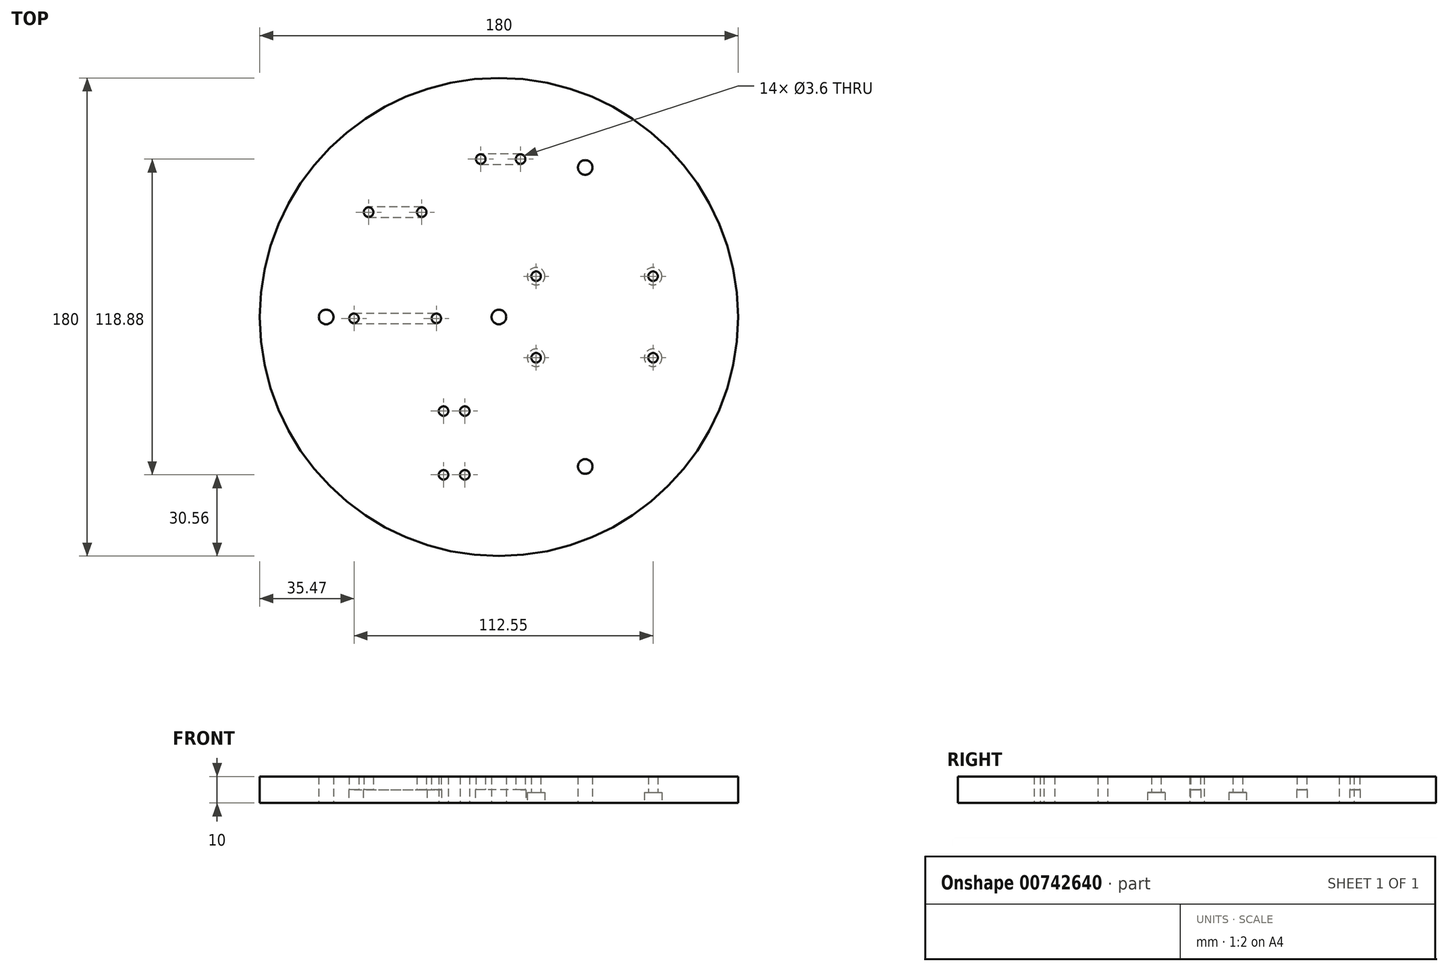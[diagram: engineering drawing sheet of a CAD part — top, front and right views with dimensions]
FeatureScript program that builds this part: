
annotation { "Feature Type Name" : "Feature", "Feature Type Description" : "" }
export const myFeature = defineFeature(function(context is Context, id is Id, definition is map)
    precondition{}
    {
        {
            var Q0;
            Q0=qCreatedBy(makeId("Top.planeOp"),FACE);
            var sketch = newSketch(context, id + "F0", { "sketchPlane" : qUnion([Q0])});
            skCircle(sketch, "E0", {"center": v(0, 0) * mm, "radius": 90 * mm});
            skLineSegment(sketch, "E1.bottom", {"start": v(22.62, 8) * mm, "end": v(49.42, 8) * mm, "construction": true});
            skLineSegment(sketch, "E1.top", {"start": v(22.62, -8) * mm, "end": v(49.42, -8) * mm, "construction": true});
            skLineSegment(sketch, "E1.left", {"start": v(22.62, 8) * mm, "end": v(22.62, -8) * mm, "construction": true});
            skLineSegment(sketch, "E1.right", {"start": v(49.42, 8) * mm, "end": v(49.42, -8) * mm, "construction": true});
            skPoint(sketch, "E1.middle", {"position": v(36.02, 0) * mm});
            skCircle(sketch, "E2", {"center": v(0, 0) * mm, "radius": 65 * mm, "construction": true});
            skPoint(sketch, "E3", {"position": v(-32.5, 56.3) * mm});
            skPoint(sketch, "E4", {"position": v(-32.5, -56.3) * mm});
            skPoint(sketch, "E5", {"position": v(65, 0) * mm});
            skPoint(sketch, "E5.positionSnap0", {"position": v(49.42, 0) * mm});
            skPoint(sketch, "E6", {"position": v(32.5, 56.3) * mm});
            skPoint(sketch, "E7", {"position": v(32.5, -56.3) * mm});
            skPoint(sketch, "E8", {"position": v(-65, 0) * mm});
            skLineSegment(sketch, "E9", {"start": v(-32.5, 56.3) * mm, "end": v(0, 0) * mm, "construction": true});
            skLineSegment(sketch, "E10", {"start": v(32.5, 56.3) * mm, "end": v(0, 0) * mm, "construction": true});
            skLineSegment(sketch, "E11", {"start": v(-65, 0) * mm, "end": v(0, 0) * mm, "construction": true});
            skLineSegment(sketch, "E12", {"start": v(-32.5, -56.3) * mm, "end": v(0, 0) * mm, "construction": true});
            skLineSegment(sketch, "E13", {"start": v(32.5, -56.3) * mm, "end": v(0, 0) * mm, "construction": true});
            skLineSegment(sketch, "E14", {"start": v(65, 0) * mm, "end": v(0, 0) * mm, "construction": true});
            skSolve(sketch);
        }
        {
            var Q0;
            Q0=qCreatedBy(makeId("Top.planeOp"),FACE);
            var sketch = newSketch(context, id + "F1", { "sketchPlane" : qUnion([Q0])});
            skLineSegment(sketch, "E15.bottom", {"start": v(-72.38, 45) * mm, "end": v(7.62, 45) * mm});
            skLineSegment(sketch, "E15.top", {"start": v(-72.38, -45) * mm, "end": v(7.62, -45) * mm});
            skLineSegment(sketch, "E15.left", {"start": v(-72.38, 45) * mm, "end": v(-72.38, -45) * mm});
            skLineSegment(sketch, "E15.right", {"start": v(7.62, 45) * mm, "end": v(7.62, -45) * mm});
            skPoint(sketch, "E16", {"position": v(-1.43, 29.7) * mm});
            skPoint(sketch, "E17", {"position": v(-1.43, -40) * mm});
            skPoint(sketch, "E18", {"position": v(-66.43, -40) * mm});
            skPoint(sketch, "E19", {"position": v(-46.03, -21.05) * mm});
            skPoint(sketch, "E20", {"position": v(-59.33, 38.95) * mm});
            skLineSegment(sketch, "E21", {"start": v(-1.43, -40) * mm, "end": v(-66.43, -40) * mm, "construction": true});
            skLineSegment(sketch, "E22", {"start": v(-66.43, -40) * mm, "end": v(-72.38, -40) * mm, "construction": true});
            skLineSegment(sketch, "E23", {"start": v(-1.43, -40) * mm, "end": v(-1.43, 29.7) * mm, "construction": true});
            skLineSegment(sketch, "E24", {"start": v(-59.33, 38.95) * mm, "end": v(-59.33, 45) * mm, "construction": true});
            skLineSegment(sketch, "E25", {"start": v(-59.33, 38.95) * mm, "end": v(-72.38, 38.95) * mm, "construction": true});
            skLineSegment(sketch, "E26", {"start": v(-46.03, -21.05) * mm, "end": v(-72.38, -21.05) * mm, "construction": true});
            skLineSegment(sketch, "E27", {"start": v(-46.03, -21.05) * mm, "end": v(-46.03, -45) * mm, "construction": true});
            skLineSegment(sketch, "E28", {"start": v(-66.43, -40) * mm, "end": v(-66.43, -45) * mm, "construction": true});
            skLineSegment(sketch, "E29", {"start": v(-1.43, 29.7) * mm, "end": v(-1.43, 45) * mm, "construction": true});
            skSolve(sketch);
        }
        {
            var Q0;
            Q0=qCreatedBy(makeId("Top.planeOp"),FACE);
            var sketch = newSketch(context, id + "F2", { "sketchPlane" : qUnion([Q0])});
            skLineSegment(sketch, "E30.bottom", {"start": v(-59.38, 49) * mm, "end": v(-6.08, 49) * mm});
            skLineSegment(sketch, "E30.top", {"start": v(-59.38, -49) * mm, "end": v(-6.08, -49) * mm});
            skLineSegment(sketch, "E30.left", {"start": v(-59.38, 49) * mm, "end": v(-59.38, -49) * mm});
            skLineSegment(sketch, "E30.right", {"start": v(-6.08, 49) * mm, "end": v(-6.08, -49) * mm});
            skPoint(sketch, "E31", {"position": v(-57, 34.97) * mm});
            skPoint(sketch, "E32", {"position": v(-8.8, 33.67) * mm});
            skPoint(sketch, "E33", {"position": v(-24, -17.13) * mm});
            skPoint(sketch, "E34", {"position": v(-51.9, -17.13) * mm});
            skPoint(sketch, "E35", {"position": v(-8.8, -41.23) * mm});
            skPoint(sketch, "E36", {"position": v(-57, -47.23) * mm});
            skSolve(sketch);
        }
        {
            var Q0;
            Q0=makeQuery(id+"F0.imprint","IMPRINT",FACE,{"disambiguationData":[TD([[makeQuery(id+"F0.imprint","IMPRINT",EDGE,{"derivedFrom":sQuery(id+"F0.wireOp",EDGE,"E0")}),1.0]])]});
            extrude(context, id + "F3", {"entities" : qUnion([Q0]), "depth" : 10 * mm, "offsetDistance" : 25 * mm});
        }
        {
            var Q0;
            Q0=sQuery(id+"F0.wireOp",VERTEX,"E6");
            var Q1;
            Q1=sQuery(id+"F0.wireOp",VERTEX,"E7");
            var Q2;
            Q2=sQuery(id+"F0.wireOp",VERTEX,"E8");
            var Q3;
            Q3=sQuery(id+"F0.wireOp",VERTEX,"E0.center");
            var Q4;
            Q4=makeQuery(id+"F3.opExtrude","SWEPT_BODY",BODY,{"disambiguationData":[OSD([sQuery(id+"F0.wireOp",EDGE,"E0")])]});
            hole(context, id + "F4", {"style" : HoleStyle.SIMPLE, "endStyle" : HoleEndStyle.BLIND, "oppositeDirection" : true, "holeDiameter" : 5.5 * mm, "majorDiameter" : 5 * mm, "holeDepth" : 30 * mm, "isTappedThrough" : true, "tappedDepth" : 10.5 * mm, "tapClearance" : 3, "locations" : qUnion([Q0, Q1, Q2, Q3]), "scope" : qUnion([Q4])});
        }
        {
            var Q0;
            Q0=makeQuery(id+"F0.imprint","IMPRINT",FACE,{"disambiguationData":[TD([[makeQuery(id+"F0.imprint","IMPRINT",EDGE,{"derivedFrom":sQuery(id+"F0.wireOp",EDGE,"E0")}),1.0]])]});
            var sketch = newSketch(context, id + "F5", { "sketchPlane" : qUnion([Q0])});
            skLineSegment(sketch, "E37.bottom", {"start": v(58.02, 15.35) * mm, "end": v(14.02, 15.35) * mm, "construction": true});
            skLineSegment(sketch, "E37.top", {"start": v(58.02, -15.35) * mm, "end": v(14.02, -15.35) * mm, "construction": true});
            skLineSegment(sketch, "E37.left", {"start": v(58.02, 15.35) * mm, "end": v(58.02, -15.35) * mm, "construction": true});
            skLineSegment(sketch, "E37.right", {"start": v(14.02, 15.35) * mm, "end": v(14.02, -15.35) * mm, "construction": true});
            skPoint(sketch, "E37.middle", {"position": v(36.02, 0) * mm});
            skSolve(sketch);
        }
        {
            var Q0;
            Q0=sQuery(id+"F5.wireOp",VERTEX,"E37.top.end");
            var Q1;
            Q1=sQuery(id+"F5.wireOp",VERTEX,"E37.top.start");
            var Q2;
            Q2=sQuery(id+"F5.wireOp",VERTEX,"E37.bottom.end");
            var Q3;
            Q3=sQuery(id+"F5.wireOp",VERTEX,"E37.bottom.start");
            var Q4;
            Q4=makeQuery(id+"F3.opExtrude","SWEPT_BODY",BODY,{"disambiguationData":[OSD([sQuery(id+"F0.wireOp",EDGE,"E0")])]});
            hole(context, id + "F6", {"style" : HoleStyle.C_BORE, "endStyle" : HoleEndStyle.THROUGH, "oppositeDirection" : true, "holeDiameter" : 3.6 * mm, "cBoreDiameter" : 6.6 * mm, "cBoreDepth" : 4 * mm, "majorDiameter" : 5 * mm, "isTappedThrough" : true, "tappedDepth" : 10.5 * mm, "tapClearance" : 3, "locations" : qUnion([Q0, Q1, Q2, Q3]), "scope" : qUnion([Q4])});
        }
        {
            var Q0;
            Q0=makeQuery(id+"F0.imprint","IMPRINT",FACE,{"disambiguationData":[TD([[makeQuery(id+"F0.imprint","IMPRINT",EDGE,{"derivedFrom":sQuery(id+"F0.wireOp",EDGE,"E0")}),1.0]])]});
            var sketch = newSketch(context, id + "F7", { "sketchPlane" : qUnion([Q0])});
            skLineSegment(sketch, "E38.bottom", {"start": v(-20.82, -35.44) * mm, "end": v(-12.82, -35.44) * mm, "construction": true});
            skLineSegment(sketch, "E38.top", {"start": v(-20.82, -59.44) * mm, "end": v(-12.82, -59.44) * mm, "construction": true});
            skLineSegment(sketch, "E38.left", {"start": v(-20.82, -35.44) * mm, "end": v(-20.82, -59.44) * mm, "construction": true});
            skLineSegment(sketch, "E38.right", {"start": v(-12.82, -35.44) * mm, "end": v(-12.82, -59.44) * mm, "construction": true});
            skPoint(sketch, "E38.middle", {"position": v(-16.82, -47.44) * mm});
            skPoint(sketch, "E39", {"position": v(-6.83, 59.44) * mm});
            skPoint(sketch, "E40", {"position": v(8.17, 59.44) * mm});
            skPoint(sketch, "E41", {"position": v(-29.03, 39.48) * mm});
            skPoint(sketch, "E42", {"position": v(-49.03, 39.48) * mm});
            skPoint(sketch, "E43", {"position": v(-54.53, -0.52) * mm});
            skPoint(sketch, "E44", {"position": v(-23.53, -0.52) * mm});
            skCircle(sketch, "E45", {"center": v(-54.53, -0.52) * mm, "radius": 2 * mm});
            skCircle(sketch, "E46", {"center": v(-23.53, -0.52) * mm, "radius": 2 * mm});
            skCircle(sketch, "E47", {"center": v(-29.03, 39.48) * mm, "radius": 2 * mm});
            skCircle(sketch, "E48", {"center": v(-49.03, 39.48) * mm, "radius": 2 * mm});
            skCircle(sketch, "E49", {"center": v(-6.83, 59.44) * mm, "radius": 2 * mm});
            skCircle(sketch, "E50", {"center": v(8.17, 59.44) * mm, "radius": 2 * mm});
            skLineSegment(sketch, "E51", {"start": v(-54.6, 1.48) * mm, "end": v(-23.53, 1.48) * mm});
            skLineSegment(sketch, "E52", {"start": v(-54.53, -2.52) * mm, "end": v(-23.53, -2.52) * mm});
            skLineSegment(sketch, "E53", {"start": v(-49.03, 37.48) * mm, "end": v(-29.03, 37.48) * mm});
            skLineSegment(sketch, "E54", {"start": v(-29.03, 41.48) * mm, "end": v(-49.03, 41.48) * mm});
            skLineSegment(sketch, "E55", {"start": v(-6.83, 57.44) * mm, "end": v(8.17, 57.44) * mm});
            skLineSegment(sketch, "E56", {"start": v(8.17, 61.44) * mm, "end": v(-6.83, 61.44) * mm});
            skSolve(sketch);
        }
        {
            var Q0;
            Q0=sQuery(id+"F7.wireOp",VERTEX,"E38.top.end");
            var Q1;
            Q1=sQuery(id+"F7.wireOp",VERTEX,"E38.top.start");
            var Q2;
            Q2=sQuery(id+"F7.wireOp",VERTEX,"E38.bottom.end");
            var Q3;
            Q3=sQuery(id+"F7.wireOp",VERTEX,"E38.bottom.start");
            var Q4;
            Q4=sQuery(id+"F7.wireOp",VERTEX,"E42");
            var Q5;
            Q5=sQuery(id+"F7.wireOp",VERTEX,"E41");
            var Q6;
            Q6=sQuery(id+"F7.wireOp",VERTEX,"E39");
            var Q7;
            Q7=sQuery(id+"F7.wireOp",VERTEX,"E40");
            var Q8;
            Q8=sQuery(id+"F7.wireOp",VERTEX,"E44");
            var Q9;
            Q9=sQuery(id+"F7.wireOp",VERTEX,"E43");
            var Q10;
            Q10=makeQuery(id+"F3.opExtrude","SWEPT_BODY",BODY,{"disambiguationData":[OSD([sQuery(id+"F0.wireOp",EDGE,"E0")])]});
            hole(context, id + "F8", {"style" : HoleStyle.SIMPLE, "endStyle" : HoleEndStyle.BLIND, "oppositeDirection" : true, "holeDiameter" : 3.6 * mm, "majorDiameter" : 5 * mm, "holeDepth" : 30 * mm, "isTappedThrough" : true, "tappedDepth" : 10.5 * mm, "tapClearance" : 3, "locations" : qUnion([Q0, Q1, Q2, Q3, Q4, Q5, Q6, Q7, Q8, Q9]), "scope" : qUnion([Q10])});
        }
        {
            var Q0;
            {var subQ0=sQuery(id+"F7.wireOp",EDGE,"E51");var subQ1=sQuery(id+"F7.wireOp",EDGE,"E45");var subQ2=makeQuery(id+"F7.imprint","INTERSECT",VERTEX,{"disambiguationData":[OD(0.0)],"derivedFrom":[subQ1,subQ0]});Q0=makeQuery(id+"F7.imprint","IMPRINT",FACE,{"disambiguationData":[TD([[makeQuery(id+"F7.imprint","IMPRINT",EDGE,{"disambiguationData":[TD([[subQ2,-1.0]])],"derivedFrom":subQ1}),1.0]])]});}
            var Q1;
            {var subQ0=sQuery(id+"F7.wireOp",EDGE,"E46");var subQ1=makeQuery(id+"F7.imprint","INTERSECT",VERTEX,{"derivedFrom":[subQ0,sQuery(id+"F7.wireOp",EDGE,"E51")]});Q1=makeQuery(id+"F7.imprint","IMPRINT",FACE,{"disambiguationData":[TD([[makeQuery(id+"F7.imprint","IMPRINT",EDGE,{"disambiguationData":[TD([[subQ1,-1.0]])],"derivedFrom":subQ0}),1.0]])]});}
            var Q2;
            {var subQ0=sQuery(id+"F7.wireOp",EDGE,"E52");Q2=makeQuery(id+"F7.imprint","IMPRINT",FACE,{"disambiguationData":[TD([[makeQuery(id+"F7.imprint","IMPRINT",EDGE,{"derivedFrom":subQ0}),1.0]])]});}
            var Q3;
            {var subQ0=sQuery(id+"F7.wireOp",EDGE,"E53");Q3=makeQuery(id+"F7.imprint","IMPRINT",FACE,{"disambiguationData":[TD([[makeQuery(id+"F7.imprint","IMPRINT",EDGE,{"derivedFrom":subQ0}),1.0]])]});}
            var Q4;
            {var subQ0=sQuery(id+"F7.wireOp",EDGE,"E48");var subQ1=makeQuery(id+"F7.imprint","INTERSECT",VERTEX,{"derivedFrom":[subQ0,sQuery(id+"F7.wireOp",EDGE,"E53")]});Q4=makeQuery(id+"F7.imprint","IMPRINT",FACE,{"disambiguationData":[TD([[makeQuery(id+"F7.imprint","IMPRINT",EDGE,{"disambiguationData":[TD([[subQ1,1.0]])],"derivedFrom":subQ0}),1.0]])]});}
            var Q5;
            {var subQ0=sQuery(id+"F7.wireOp",EDGE,"E47");var subQ1=makeQuery(id+"F7.imprint","INTERSECT",VERTEX,{"derivedFrom":[subQ0,sQuery(id+"F7.wireOp",EDGE,"E53")]});Q5=makeQuery(id+"F7.imprint","IMPRINT",FACE,{"disambiguationData":[TD([[makeQuery(id+"F7.imprint","IMPRINT",EDGE,{"disambiguationData":[TD([[subQ1,1.0]])],"derivedFrom":subQ0}),1.0]])]});}
            var Q6;
            {var subQ0=sQuery(id+"F7.wireOp",EDGE,"E55");Q6=makeQuery(id+"F7.imprint","IMPRINT",FACE,{"disambiguationData":[TD([[makeQuery(id+"F7.imprint","IMPRINT",EDGE,{"derivedFrom":subQ0}),1.0]])]});}
            var Q7;
            {var subQ0=sQuery(id+"F7.wireOp",EDGE,"E49");var subQ1=makeQuery(id+"F7.imprint","INTERSECT",VERTEX,{"derivedFrom":[subQ0,sQuery(id+"F7.wireOp",EDGE,"E55")]});Q7=makeQuery(id+"F7.imprint","IMPRINT",FACE,{"disambiguationData":[TD([[makeQuery(id+"F7.imprint","IMPRINT",EDGE,{"disambiguationData":[TD([[subQ1,1.0]])],"derivedFrom":subQ0}),1.0]])]});}
            var Q8;
            {var subQ0=sQuery(id+"F7.wireOp",EDGE,"E50");var subQ1=makeQuery(id+"F7.imprint","INTERSECT",VERTEX,{"derivedFrom":[subQ0,sQuery(id+"F7.wireOp",EDGE,"E55")]});Q8=makeQuery(id+"F7.imprint","IMPRINT",FACE,{"disambiguationData":[TD([[makeQuery(id+"F7.imprint","IMPRINT",EDGE,{"disambiguationData":[TD([[subQ1,1.0]])],"derivedFrom":subQ0}),1.0]])]});}
            extrude(context, id + "F9", {"entities" : qUnion([Q0, Q1, Q2, Q3, Q4, Q5, Q6, Q7, Q8]), "operationType" : NewBodyOperationType.REMOVE, "depth" : 5 * mm, "offsetDistance" : 25 * mm});
        }
    });
